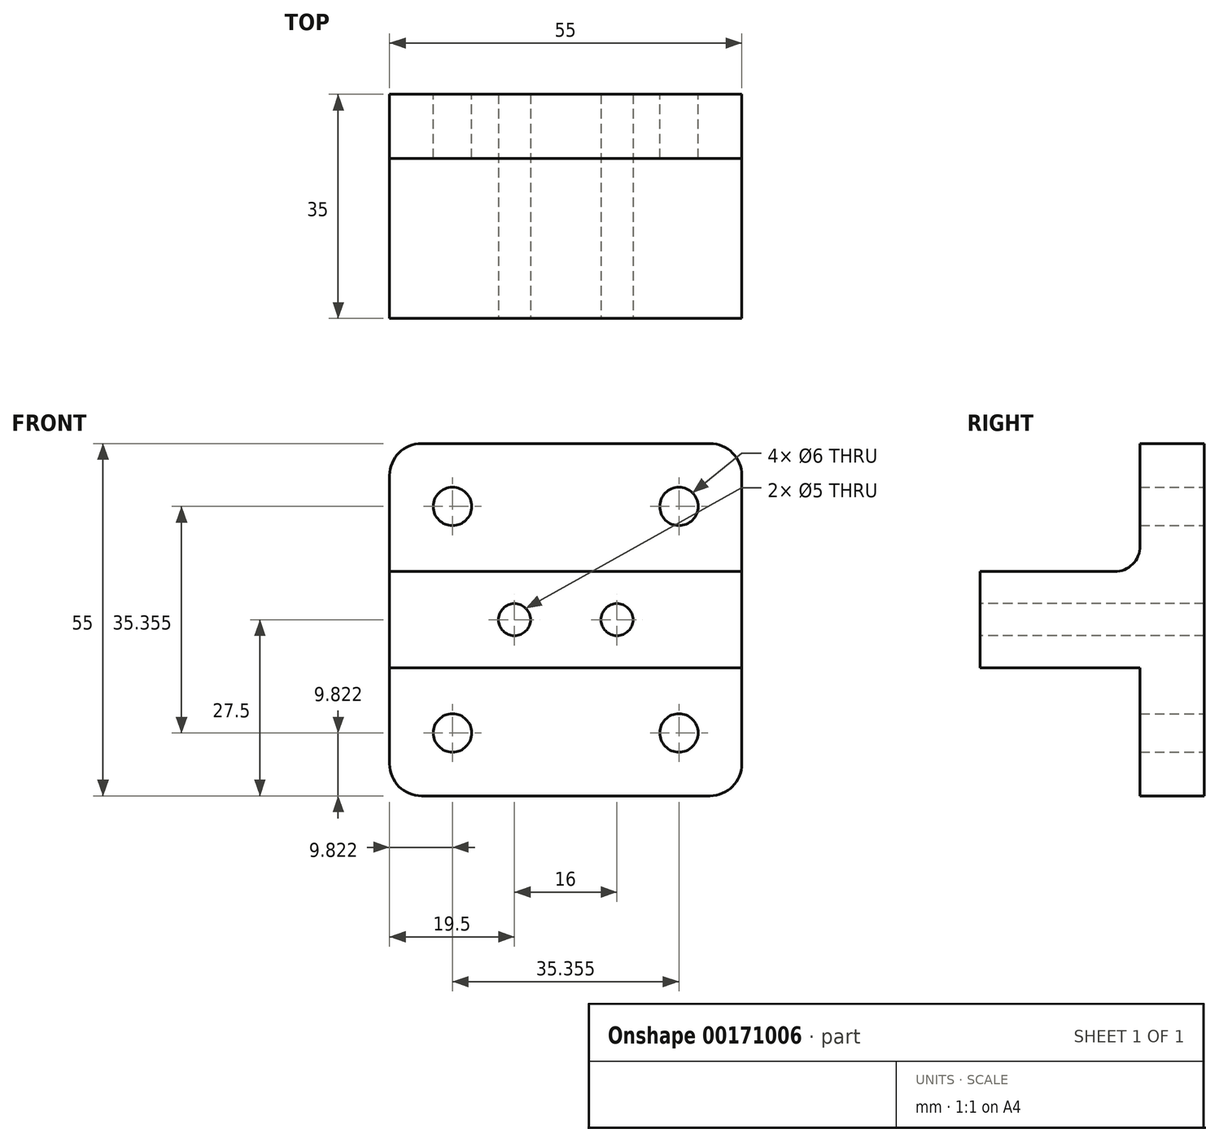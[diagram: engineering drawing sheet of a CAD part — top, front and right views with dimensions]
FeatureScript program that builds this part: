
annotation { "Feature Type Name" : "Feature", "Feature Type Description" : "" }
export const myFeature = defineFeature(function(context is Context, id is Id, definition is map)
    precondition{}
    {
        {
            var Q0;
            Q0=qCreatedBy(makeId("Front.planeOp"),FACE);
            var sketch = newSketch(context, id + "F0", { "sketchPlane" : qUnion([Q0])});
            skCircle(sketch, "E0", {"center": v(0, 0) * mm, "radius": 25 * mm, "construction": true});
            skLineSegment(sketch, "E1.bottom", {"start": v(27.5, -27.5) * mm, "end": v(-27.5, -27.5) * mm});
            skLineSegment(sketch, "E1.top", {"start": v(27.5, 27.5) * mm, "end": v(-27.5, 27.5) * mm});
            skLineSegment(sketch, "E1.left", {"start": v(27.5, -27.5) * mm, "end": v(27.5, 27.5) * mm});
            skLineSegment(sketch, "E1.right", {"start": v(-27.5, -27.5) * mm, "end": v(-27.5, 27.5) * mm});
            skCircle(sketch, "E2", {"center": v(-17.68, 17.68) * mm, "radius": 3 * mm});
            skCircle(sketch, "E3", {"center": v(17.68, 17.68) * mm, "radius": 3 * mm});
            skCircle(sketch, "E4", {"center": v(17.68, -17.68) * mm, "radius": 3 * mm});
            skCircle(sketch, "E5", {"center": v(-17.68, -17.68) * mm, "radius": 3 * mm});
            skLineSegment(sketch, "E6", {"start": v(-17.68, 17.68) * mm, "end": v(0, 0) * mm, "construction": true});
            skLineSegment(sketch, "E7", {"start": v(0, 0) * mm, "end": v(17.68, 17.68) * mm, "construction": true});
            skLineSegment(sketch, "E8", {"start": v(0, 0) * mm, "end": v(17.68, -17.68) * mm, "construction": true});
            skLineSegment(sketch, "E9", {"start": v(0, 0) * mm, "end": v(-17.68, -17.68) * mm, "construction": true});
            skSolve(sketch);
        }
        {
            var Q0;
            Q0=makeQuery(id+"F0.imprint","IMPRINT",FACE,{"disambiguationData":[TD([[makeQuery(id+"F0.imprint","IMPRINT",EDGE,{"derivedFrom":sQuery(id+"F0.wireOp",EDGE,"E1.bottom")}),-1.0]])]});
            extrude(context, id + "F1", {"entities" : qUnion([Q0]), "depth" : 10 * mm});
        }
        {
            var Q0;
            Q0=makeQuery(id+"F1.opExtrude","SWEPT_EDGE",EDGE,{"disambiguationData":[OSD([sQuery(id+"F0.wireOp",EDGE,"E1.top"),sQuery(id+"F0.wireOp",EDGE,"E1.right")])]});
            var Q1;
            Q1=makeQuery(id+"F1.opExtrude","SWEPT_EDGE",EDGE,{"disambiguationData":[OSD([sQuery(id+"F0.wireOp",EDGE,"E1.bottom"),sQuery(id+"F0.wireOp",EDGE,"E1.right")])]});
            var Q2;
            Q2=makeQuery(id+"F1.opExtrude","SWEPT_EDGE",EDGE,{"disambiguationData":[OSD([sQuery(id+"F0.wireOp",EDGE,"E1.top"),sQuery(id+"F0.wireOp",EDGE,"E1.left")])]});
            var Q3;
            Q3=makeQuery(id+"F1.opExtrude","SWEPT_EDGE",EDGE,{"disambiguationData":[OSD([sQuery(id+"F0.wireOp",EDGE,"E1.bottom"),sQuery(id+"F0.wireOp",EDGE,"E1.left")])]});
            fillet(context, id + "F2", {"entities" : qUnion([Q0, Q1, Q2, Q3]), "radius" : 5 * mm, "tangentPropagation" : true, "allowEdgeOverflow" : false});
        }
        {
            var Q0;
            Q0=makeQuery(id+"F1.opExtrude","SWEPT_FACE",FACE,{"disambiguationData":[OSD([sQuery(id+"F0.wireOp",EDGE,"E1.left")])]});
            var sketch = newSketch(context, id + "F3", { "sketchPlane" : qUnion([Q0])});
            skLineSegment(sketch, "E10.bottom", {"start": v(-10, 7.5) * mm, "end": v(-35, 7.5) * mm});
            skLineSegment(sketch, "E10.top", {"start": v(-10, -7.5) * mm, "end": v(-35, -7.5) * mm});
            skLineSegment(sketch, "E10.left", {"start": v(-10, 7.5) * mm, "end": v(-10, -7.5) * mm});
            skLineSegment(sketch, "E10.right", {"start": v(-35, 7.5) * mm, "end": v(-35, -7.5) * mm});
            skPoint(sketch, "E10.middle", {"position": v(-22.5, 0) * mm});
            skSolve(sketch);
        }
        {
            var Q0;
            Q0 = qSketchRegion(id + "F3", true);
            extrude(context, id + "F4", {"entities" : qUnion([Q0]), "operationType" : NewBodyOperationType.ADD, "oppositeDirection" : true, "depth" : 55 * mm});
        }
        {
            var Q0;
            Q0=makeQuery(id+"F1.opExtrude","CAP_FACE",FACE,{"disambiguationData":[OSD([sQuery(id+"F0.wireOp",EDGE,"E1.bottom"),sQuery(id+"F0.wireOp",EDGE,"E1.top"),sQuery(id+"F0.wireOp",EDGE,"E1.left"),sQuery(id+"F0.wireOp",EDGE,"E1.right"),sQuery(id+"F0.wireOp",EDGE,"E2"),sQuery(id+"F0.wireOp",EDGE,"E3"),sQuery(id+"F0.wireOp",EDGE,"E4"),sQuery(id+"F0.wireOp",EDGE,"E5")])],"isStart":false});
            var sketch = newSketch(context, id + "F5", { "sketchPlane" : qUnion([Q0])});
            skCircle(sketch, "E11", {"center": v(8, 0) * mm, "radius": 2.5 * mm});
            skCircle(sketch, "E12", {"center": v(-8, 0) * mm, "radius": 2.5 * mm});
            skSolve(sketch);
        }
        {
            var Q0;
            Q0 = qSketchRegion(id + "F5", true);
            extrude(context, id + "F6", {"entities" : qUnion([Q0]), "operationType" : NewBodyOperationType.REMOVE, "endBound" : BoundingType.THROUGH_ALL, "oppositeDirection" : true, "depth" : 25 * mm, "hasSecondDirection" : true, "secondDirectionBound" : SecondDirectionBoundingType.THROUGH_ALL, "secondDirectionOppositeDirection" : false, "secondDirectionDepth" : 25 * mm});
        }
        {
            var Q0;
            Q0=makeQuery(id+"F4.opExtrude","SWEPT_EDGE",EDGE,{"disambiguationData":[OSD([sQuery(id+"F0.wireOp",EDGE,"E1.left"),sQuery(id+"F3.wireOp",EDGE,"E10.top"),sQuery(id+"F3.wireOp",EDGE,"E10.left")])]});
            var Q1;
            Q1=makeQuery(id+"F4.opExtrude","SWEPT_EDGE",EDGE,{"disambiguationData":[OSD([sQuery(id+"F0.wireOp",EDGE,"E1.left"),sQuery(id+"F3.wireOp",EDGE,"E10.bottom"),sQuery(id+"F3.wireOp",EDGE,"E10.left")])]});
            fillet(context, id + "F7", {"entities" : qUnion([Q0, Q1]), "radius" : 4 * mm, "tangentPropagation" : true, "allowEdgeOverflow" : false});
        }
    });
